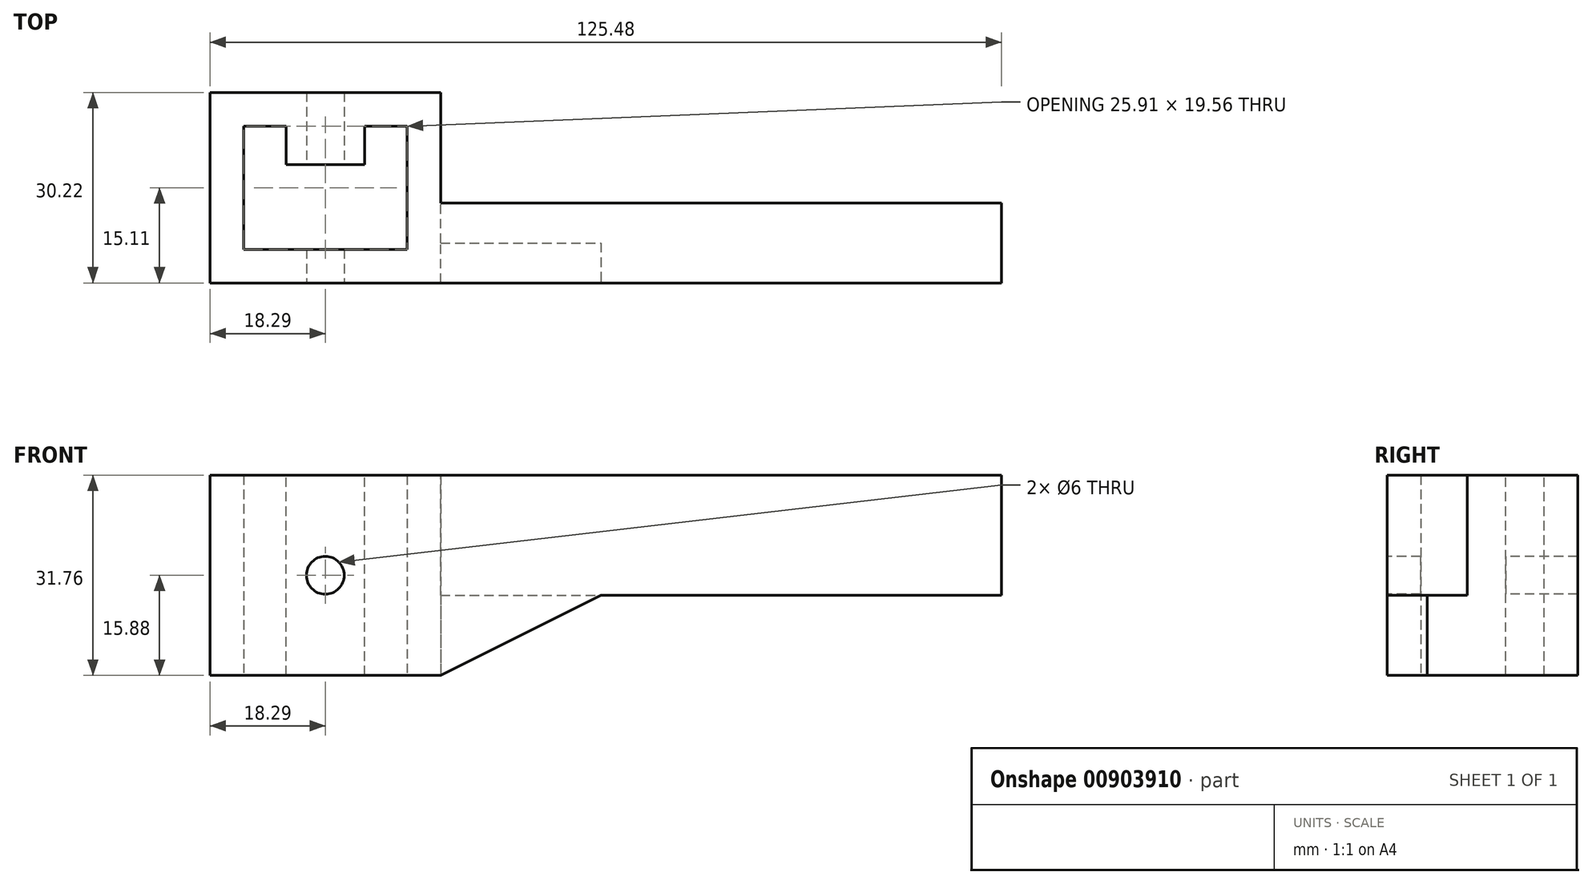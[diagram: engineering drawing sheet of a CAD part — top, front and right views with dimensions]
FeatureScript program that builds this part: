
annotation { "Feature Type Name" : "Feature", "Feature Type Description" : "" }
export const myFeature = defineFeature(function(context is Context, id is Id, definition is map)
    precondition{}
    {
        {
            var Q0;
            Q0=qCreatedBy(makeId("Top.planeOp"),FACE);
            var sketch = newSketch(context, id + "F0", { "sketchPlane" : qUnion([Q0])});
            skLineSegment(sketch, "E0.bottom", {"start": v(12.95, -9.78) * mm, "end": v(-12.95, -9.78) * mm});
            skLineSegment(sketch, "E0.top", {"start": v(12.95, 9.78) * mm, "end": v(-12.95, 9.78) * mm});
            skLineSegment(sketch, "E0.left", {"start": v(12.95, -9.78) * mm, "end": v(12.95, 9.78) * mm});
            skLineSegment(sketch, "E0.right", {"start": v(-12.95, -9.78) * mm, "end": v(-12.95, 9.78) * mm});
            skPoint(sketch, "E0.middle", {"position": v(0, 0) * mm});
            skLineSegment(sketch, "E1.0", {"start": v(-18.29, -15.11) * mm, "end": v(-18.29, 15.11) * mm});
            skLineSegment(sketch, "E1.1", {"start": v(18.29, -15.11) * mm, "end": v(-18.29, -15.11) * mm});
            skLineSegment(sketch, "E1.2", {"start": v(18.29, -15.11) * mm, "end": v(18.29, 15.11) * mm});
            skLineSegment(sketch, "E1.3", {"start": v(18.29, 15.11) * mm, "end": v(-18.29, 15.11) * mm});
            skSolve(sketch);
        }
        {
            var Q0;
            Q0=makeQuery(id+"F0.imprint","IMPRINT",FACE,{"disambiguationData":[TD([[makeQuery(id+"F0.imprint","IMPRINT",EDGE,{"derivedFrom":sQuery(id+"F0.wireOp",EDGE,"E0.bottom")}),1.0]])]});
            extrude(context, id + "F1", {"entities" : qUnion([Q0]), "endBound" : BoundingType.SYMMETRIC, "depth" : 31.75 * mm, "offsetDistance" : 25.4 * mm});
        }
        {
            var Q0;
            Q0=makeQuery(id+"F1.opExtrude","CAP_FACE",FACE,{"disambiguationData":[OSD([sQuery(id+"F0.wireOp",EDGE,"E0.bottom"),sQuery(id+"F0.wireOp",EDGE,"E0.top"),sQuery(id+"F0.wireOp",EDGE,"E0.left"),sQuery(id+"F0.wireOp",EDGE,"E0.right"),sQuery(id+"F0.wireOp",EDGE,"E1.0"),sQuery(id+"F0.wireOp",EDGE,"E1.1"),sQuery(id+"F0.wireOp",EDGE,"E1.2"),sQuery(id+"F0.wireOp",EDGE,"E1.3")])],"isStart":false});
            var sketch = newSketch(context, id + "F2", { "sketchPlane" : qUnion([Q0])});
            skLineSegment(sketch, "E2.bottom", {"start": v(6.22, 9.78) * mm, "end": v(-6.22, 9.78) * mm});
            skLineSegment(sketch, "E2.top", {"start": v(6.22, 3.68) * mm, "end": v(-6.22, 3.68) * mm});
            skLineSegment(sketch, "E2.left", {"start": v(6.22, 9.78) * mm, "end": v(6.22, 3.68) * mm});
            skLineSegment(sketch, "E2.right", {"start": v(-6.22, 9.78) * mm, "end": v(-6.22, 3.68) * mm});
            skPoint(sketch, "E2.middle", {"position": v(0, 6.73) * mm});
            skPoint(sketch, "E2.middle.positionSnap0", {"position": v(0, 9.78) * mm});
            skPoint(sketch, "E2.centerSnap0", {"position": v(0, 9.78) * mm});
            skSolve(sketch);
        }
        {
            var Q0;
            Q0=makeQuery(id+"F2.imprint","IMPRINT",FACE,{"disambiguationData":[TD([[makeQuery(id+"F2.imprint","IMPRINT",EDGE,{"derivedFrom":sQuery(id+"F2.wireOp",EDGE,"E2.bottom")}),1.0]])]});
            extrude(context, id + "F3", {"entities" : qUnion([Q0]), "operationType" : NewBodyOperationType.ADD, "oppositeDirection" : true, "depth" : 31.75 * mm, "offsetDistance" : 25.4 * mm});
        }
        {
            var Q0;
            Q0=makeQuery(id+"F3.boolean.opBoolean","MERGE",FACE,{"derivedFrom":[makeQuery(id+"F1.opExtrude","CAP_FACE",FACE,{"disambiguationData":[OSD([sQuery(id+"F0.wireOp",EDGE,"E0.bottom"),sQuery(id+"F0.wireOp",EDGE,"E0.top"),sQuery(id+"F0.wireOp",EDGE,"E0.left"),sQuery(id+"F0.wireOp",EDGE,"E0.right"),sQuery(id+"F0.wireOp",EDGE,"E1.0"),sQuery(id+"F0.wireOp",EDGE,"E1.1"),sQuery(id+"F0.wireOp",EDGE,"E1.2"),sQuery(id+"F0.wireOp",EDGE,"E1.3")])],"isStart":false}),makeQuery(id+"F3.opExtrude","CAP_FACE",FACE,{"disambiguationData":[OSD([sQuery(id+"F2.wireOp",EDGE,"E2.bottom"),sQuery(id+"F2.wireOp",EDGE,"E2.top"),sQuery(id+"F2.wireOp",EDGE,"E2.left"),sQuery(id+"F2.wireOp",EDGE,"E2.right")])],"isStart":true})]});
            var sketch = newSketch(context, id + "F4", { "sketchPlane" : qUnion([Q0])});
            skLineSegment(sketch, "E3.bottom", {"start": v(18.29, -15.11) * mm, "end": v(107.19, -15.11) * mm});
            skLineSegment(sketch, "E3.top", {"start": v(18.29, -2.41) * mm, "end": v(107.19, -2.41) * mm});
            skLineSegment(sketch, "E3.left", {"start": v(18.29, -15.11) * mm, "end": v(18.29, -2.41) * mm});
            skLineSegment(sketch, "E3.right", {"start": v(107.19, -15.11) * mm, "end": v(107.19, -2.41) * mm});
            skSolve(sketch);
        }
        {
            var Q0;
            Q0=makeQuery(id+"F4.imprint","IMPRINT",FACE,{"disambiguationData":[TD([[makeQuery(id+"F4.imprint","IMPRINT",EDGE,{"derivedFrom":sQuery(id+"F4.wireOp",EDGE,"E3.bottom")}),1.0]])]});
            extrude(context, id + "F5", {"entities" : qUnion([Q0]), "operationType" : NewBodyOperationType.ADD, "oppositeDirection" : true, "depth" : 19.05 * mm, "offsetDistance" : 25.4 * mm});
        }
        {
            var Q0;
            Q0=makeQuery(id+"F5.boolean.opBoolean","MERGE",FACE,{"derivedFrom":[makeQuery(id+"F1.opExtrude","SWEPT_FACE",FACE,{"disambiguationData":[OSD([sQuery(id+"F0.wireOp",EDGE,"E1.1")])]}),makeQuery(id+"F5.opExtrude","SWEPT_FACE",FACE,{"disambiguationData":[OSD([sQuery(id+"F4.wireOp",EDGE,"E3.bottom")])]})]});
            var sketch = newSketch(context, id + "F6", { "sketchPlane" : qUnion([Q0])});
            skLineSegment(sketch, "E4", {"start": v(18.29, -3.18) * mm, "end": v(43.69, -3.18) * mm});
            skLineSegment(sketch, "E5", {"start": v(43.69, -3.17) * mm, "end": v(18.29, -15.88) * mm});
            skLineSegment(sketch, "E6", {"start": v(18.29, -15.88) * mm, "end": v(18.29, -3.18) * mm});
            skSolve(sketch);
        }
        {
            var Q0;
            Q0=qSketchRegion(id+"F6",true);
            extrude(context, id + "F7", {"entities" : qUnion([Q0]), "operationType" : NewBodyOperationType.ADD, "oppositeDirection" : true, "depth" : 6.35 * mm, "offsetDistance" : 25.4 * mm});
        }
        {
            var Q0;
            Q0=makeQuery(id+"F7.boolean.opBoolean","MERGE",FACE,{"derivedFrom":[makeQuery(id+"F5.boolean.opBoolean","MERGE",FACE,{"derivedFrom":[makeQuery(id+"F1.opExtrude","SWEPT_FACE",FACE,{"disambiguationData":[OSD([sQuery(id+"F0.wireOp",EDGE,"E1.1")])]}),makeQuery(id+"F5.opExtrude","SWEPT_FACE",FACE,{"disambiguationData":[OSD([sQuery(id+"F4.wireOp",EDGE,"E3.bottom")])]})]}),makeQuery(id+"F7.opExtrude","CAP_FACE",FACE,{"disambiguationData":[OSD([sQuery(id+"F6.wireOp",EDGE,"E4"),sQuery(id+"F6.wireOp",EDGE,"E5"),sQuery(id+"F6.wireOp",EDGE,"E6")])],"isStart":true})]});
            var sketch = newSketch(context, id + "F8", { "sketchPlane" : qUnion([Q0])});
            skCircle(sketch, "E7", {"center": v(0, 0) * mm, "radius": 3 * mm});
            skSolve(sketch);
        }
        {
            var Q0;
            Q0=qSketchRegion(id+"F8",true);
            extrude(context, id + "F9", {"entities" : qUnion([Q0]), "operationType" : NewBodyOperationType.REMOVE, "endBound" : BoundingType.THROUGH_ALL, "oppositeDirection" : true, "depth" : 25.4 * mm, "offsetDistance" : 25.4 * mm});
        }
    });
